# Revit family: Be- u. Entlüfter inkl. RV 2630 00 (01)
name_source: partatom
category: Rohrzubehör
units: mm (PartAtom-declared; Revit-internal decimal feet)

## family parameters
Arbeitsebenenbasiert = Nein
Beim Laden mit Abzugskörper schneiden = Nein
Bemaßung runder Anschluss = Durchmesser verwenden
Gemeinsam genutzt = Nein
Immer vertikal = Ja
OmniClass-Nummer = 23.65.55.14
OmniClass-Titel = Valves for Liquid Services
Teiletyp = Normal

## types (1)
- Be- u. Entlüfter inkl. RV 2630 00 (01)
    Abdeckkappe = Polypropylen, Schwarz
    Anwendungsgebiet = Der automatische Schnellentlüfter wird in Heizungs- und Kühlungssysteme zur Entlüftung der Anlage verwendet. Das Ventil sollte in der Nähe des Boilers oder am höchsten Punkt der Anlage installiert werden, um eine garantierte Entlüftung der Anlage an die Umgebung zu gewährleisten.
    Aussengewindeanschluss = nach ISO 228
    D01 = 16.2 mm  [stored 0.0531496 ft]
    D02 = 19.5 mm  [stored 0.0639764 ft]
    D03 = 5.1 mm  [stored 0.0167323 ft]
    D04 = 3.4 mm
    D05 = 0.8 mm
    D06 = 4 mm  [stored 0.0131234 ft]
    D07 = 11.5 mm  [stored 0.0377297 ft]
    Deckel = geschmiedetes Messing nach EN 12165, CW617N
    Dichtung = NBR
    G = 5 mm  [stored 0.0164042 ft]
    Gehäuse = geschmiedetes Messing nach EN 12165, CW617N
    H00 = 59 mm
    H01 = 12 mm  [stored 0.0393701 ft]
    H02 = 9.5 mm  [stored 0.031168 ft]
    H03 = 63 mm
    H04 = 57.9 mm
    H05 = 58 mm  [stored 0.190289 ft]
    H06 = 25.3 mm  [stored 0.0830052 ft]
    H07 = 9.8 mm  [stored 0.0321522 ft]
    H08 = 13.2 mm  [stored 0.0433071 ft]
    Hersteller = Herz-Armaturen GmbH
    L00 = 33.5 mm
    L01 = 9.5 mm  [stored 0.031168 ft]
    L02 = 4.8 mm  [stored 0.015748 ft]
    L03 = 13.5 mm
    L04 = 24 mm  [stored 0.0787402 ft]
    Max.Betriebsdruck = 800000.0 Pa
    Max.Betriebstemperatur = 110 °C
    Max.Strukturdruck = 1200000.0 Pa
    Medium = Heizungswasser nach ÖNORM H5195 oder VDI- Richtlinie 2035. Die Verwendung von Ethylen- oder Propyleneglykol in einem Mischungsverhältnis von 25 - 50% ist zulässig. EPDM-Dichtungen können durch Mineralöle und Schmiermittel beeinflusst werden, was zum Versagen der EPDM-Dichtungen führen kann. Bitte beachten Sie die Dokumentation des Herstellers, wenn Ethylenglykol-Produkte für den Frost- und Korrosionsschutz verwendet werden.
    Min.Betriebstemperatur = 0 °C
    R01 = 2 mm  [stored 0.00656168 ft]
    Rückflussverhinderer = Messing CW617N, EN 12165
    S01 = 59 mm
    S02 = 24.5 mm
    S03 = 11 mm  [stored 0.0360892 ft]
    S04 = 21 mm  [stored 0.0688976 ft]
    S05 = 25.3 mm  [stored 0.0830052 ft]
    SCRNCODE = 05;14;01
    SCRNSEQ = AWI;AWI_TYP="1013";1
    SW = 10.5 mm  [stored 0.0344488 ft]
    Schwimmer = Polypropylen
    URL = www.herz-armaturen.at
    Vorgabe-Ansicht = 0 mm  [stored 0 ft]

note: [stored X ft] marks values corroborated as IEEE doubles in the binary element streams (Revit-internal decimal feet)
